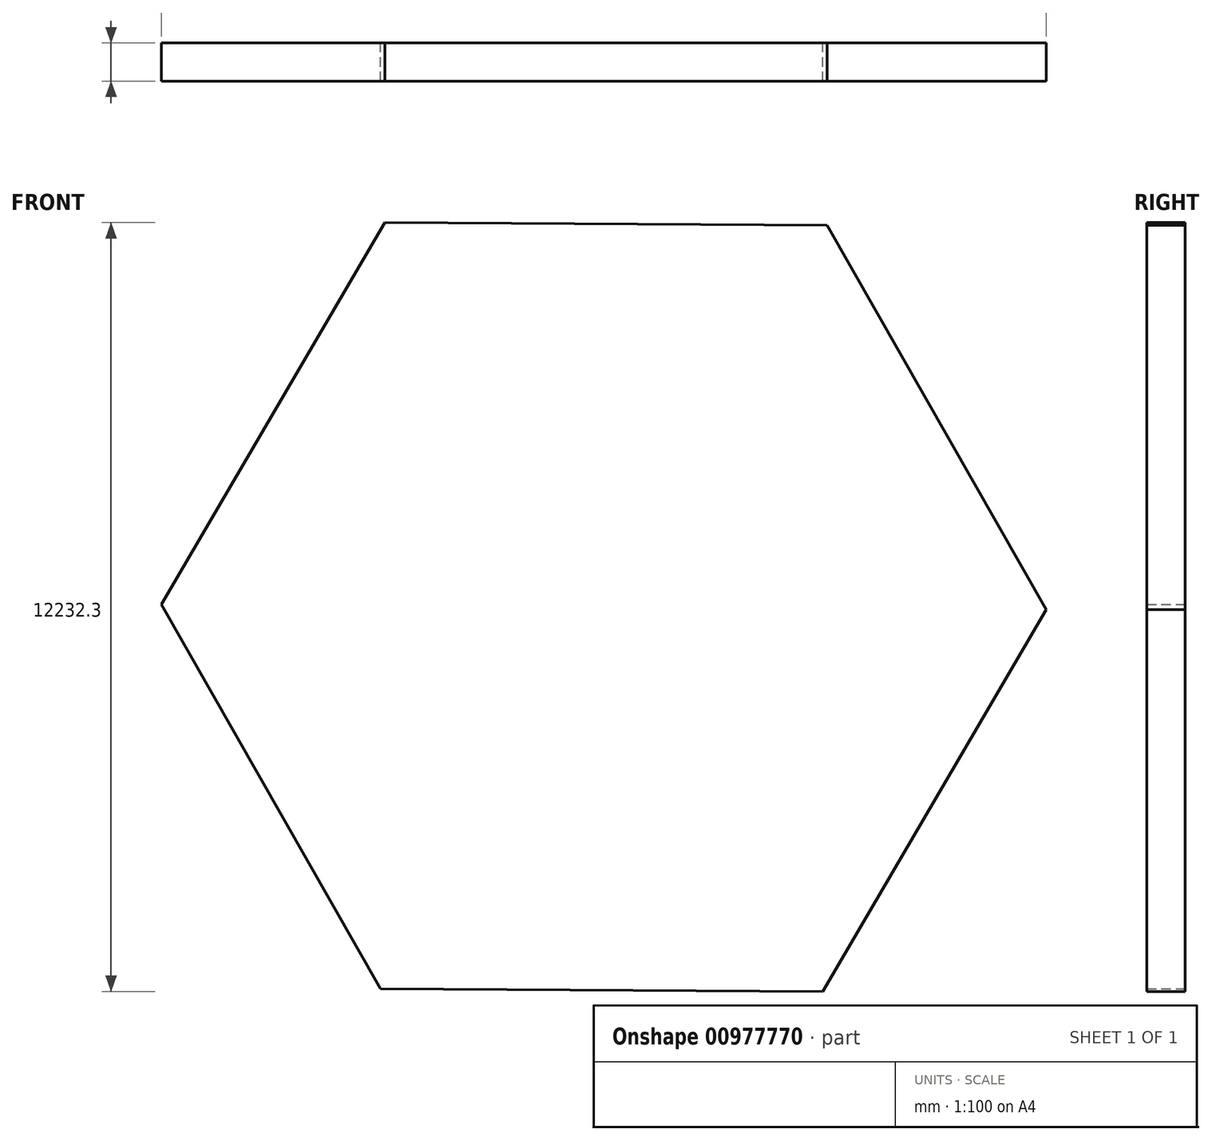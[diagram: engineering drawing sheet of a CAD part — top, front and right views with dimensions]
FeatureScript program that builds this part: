
annotation { "Feature Type Name" : "Feature", "Feature Type Description" : "" }
export const myFeature = defineFeature(function(context is Context, id is Id, definition is map)
    precondition{}
    {
        {
            var Q0;
            Q0=qCreatedBy(makeId("Front.planeOp"),FACE);
            var sketch = newSketch(context, id + "F0", { "sketchPlane" : qUnion([Q0])});
            skCircle(sketch, "E0.cCircle", {"center": v(0, 0) * mm, "radius": 6096.1 * mm, "construction": true});
            skLineSegment(sketch, "E0.0", {"start": v(7039.05, -40.25) * mm, "end": v(3484.67, -6116.13) * mm});
            skLineSegment(sketch, "E0.1", {"start": v(3484.67, -6116.13) * mm, "end": v(-3554.39, -6075.87) * mm});
            skLineSegment(sketch, "E0.2", {"start": v(-3554.39, -6075.87) * mm, "end": v(-7039.05, 40.25) * mm});
            skLineSegment(sketch, "E0.3", {"start": v(-7039.05, 40.25) * mm, "end": v(-3484.67, 6116.13) * mm});
            skLineSegment(sketch, "E0.4", {"start": v(-3484.67, 6116.13) * mm, "end": v(3554.39, 6075.87) * mm});
            skLineSegment(sketch, "E0.5", {"start": v(3554.39, 6075.87) * mm, "end": v(7039.05, -40.25) * mm});
            skPoint(sketch, "E0.0.midPoint", {"position": v(5261.86, -3078.19) * mm});
            skSolve(sketch);
        }
        {
            var Q0;
            Q0 = qSketchRegion(id + "F0", true);
            extrude(context, id + "F1", {"entities" : qUnion([Q0]), "endBound" : BoundingType.SYMMETRIC, "depth" : 609.6 * mm, "offsetDistance" : 25.4 * mm});
        }
    });
